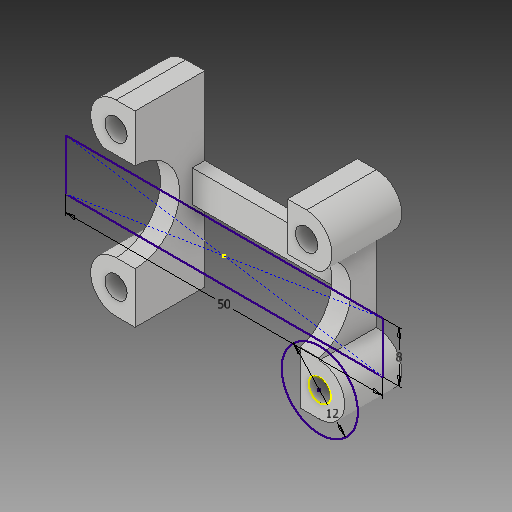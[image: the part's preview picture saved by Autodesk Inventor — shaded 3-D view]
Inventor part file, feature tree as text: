
AUTODESK INVENTOR PART (.ipt)
format: ipt  version: 2019 (Build 230136000, 136)  size: 185,856 bytes
history: native  units: mm
features: reference x8, sketch x5, extrude x4, other x3, projected_geometry x1
ambient origin geometry x8: Origin, YZ Plane, XZ Plane, XY Plane, X Axis, Y Axis, Z Axis, Center Point
bodies: Body1 (feature_tree)
feature tree (21):
  other  "Твердое тело1"
  extrude  "Выдавливание1"  Depth=3.0mm
  extrude  "Выдавливание2"  Depth=11.0mm TaperAngle=0.0deg
  extrude  "Выдавливание3"  Depth=6.0mm
  extrude  "Выдавливание4"  Depth=7.0mm
  sketch  "Эскиз6"
  sketch  "Эскиз1"
  reference  "Ссылка1"
  reference  "Ссылка2"
  reference  "Ссылка3"
  reference  "Ссылка4"
  reference  "Ссылка5"
  reference  "Ссылка6"
  reference  "Ссылка7"
  reference  "Ссылка8"
  sketch  "Эскиз2"
  sketch  "Эскиз3"
  sketch  "Эскиз5"
  projected_geometry  "Спроецированная петля1"
  other  "Infrared sensor.iam"
  other  "Base:1"
